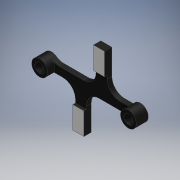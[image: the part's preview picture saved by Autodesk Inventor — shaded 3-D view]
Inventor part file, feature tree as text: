
AUTODESK INVENTOR PART (.ipt)
format: ipt  version: 2018 (Build 220112000, 112)  size: 134,144 bytes
history: native  units: mm
features: fillet x1
ambient origin geometry x8: Origin, YZ Plane, XZ Plane, XY Plane, X Axis, Y Axis, Z Axis, Center Point
bodies: Solid1 (feature_tree)
feature tree (1):
  fillet  "Fillet1"  [1 undecoded]
note: 1 required parameter value undecoded (feature->parameter linkage not recoverable at this tier; creation-order binding heuristic only, values carry confidence <= 0.55)
